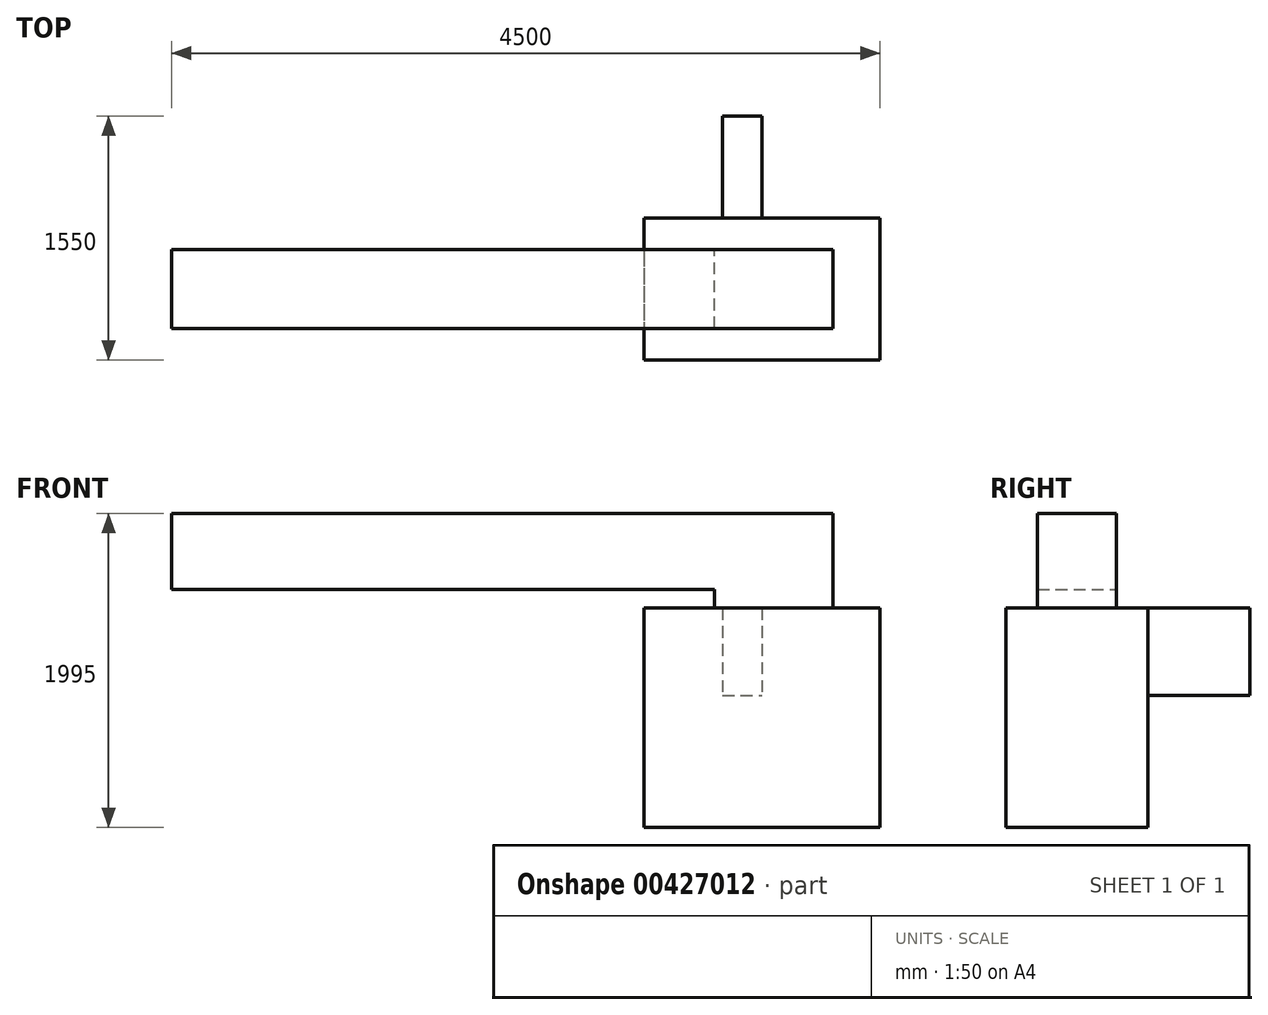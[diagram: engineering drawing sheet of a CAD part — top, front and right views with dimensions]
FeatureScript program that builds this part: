
annotation { "Feature Type Name" : "Feature", "Feature Type Description" : "" }
export const myFeature = defineFeature(function(context is Context, id is Id, definition is map)
    precondition{}
    {
        {
            var Q0;
            Q0=qCreatedBy(makeId("Top.planeOp"),FACE);
            var sketch = newSketch(context, id + "F0", { "sketchPlane" : qUnion([Q0])});
            skLineSegment(sketch, "E0.bottom", {"start": v(-750, 450) * mm, "end": v(750, 450) * mm});
            skLineSegment(sketch, "E0.top", {"start": v(-750, -450) * mm, "end": v(750, -450) * mm});
            skLineSegment(sketch, "E0.left", {"start": v(-750, 450) * mm, "end": v(-750, -450) * mm});
            skLineSegment(sketch, "E0.right", {"start": v(750, 450) * mm, "end": v(750, -450) * mm});
            skSolve(sketch);
        }
        {
            var Q0;
            Q0=makeQuery(id+"F0.imprint","IMPRINT",FACE,{"disambiguationData":[TD([[makeQuery(id+"F0.imprint","IMPRINT",EDGE,{"derivedFrom":sQuery(id+"F0.wireOp",EDGE,"E0.bottom")}),-1.0]])]});
            extrude(context, id + "F1", {"entities" : qUnion([Q0]), "endBound" : BoundingType.SYMMETRIC, "depth" : (840 + 555) * mm});
        }
        {
            var Q0;
            Q0=makeQuery(id+"F1.opExtrude","SWEPT_FACE",FACE,{"disambiguationData":[OSD([sQuery(id+"F0.wireOp",EDGE,"E0.bottom")])]});
            var sketch = newSketch(context, id + "F2", { "sketchPlane" : qUnion([Q0])});
            skLineSegment(sketch, "E1.bottom", {"start": v(250, 697.5) * mm, "end": v(0, 697.5) * mm});
            skLineSegment(sketch, "E1.top", {"start": v(250, 142.5) * mm, "end": v(0, 142.5) * mm});
            skLineSegment(sketch, "E1.left", {"start": v(250, 697.5) * mm, "end": v(250, 142.5) * mm});
            skLineSegment(sketch, "E1.right", {"start": v(0, 697.5) * mm, "end": v(0, 142.5) * mm});
            skSolve(sketch);
        }
        {
            var Q0;
            Q0=makeQuery(id+"F2.imprint","IMPRINT",FACE,{"disambiguationData":[TD([[makeQuery(id+"F2.imprint","IMPRINT",EDGE,{"derivedFrom":sQuery(id+"F2.wireOp",EDGE,"E1.bottom")}),1.0]])]});
            extrude(context, id + "F3", {"entities" : qUnion([Q0]), "depth" : 650 * mm});
        }
        {
            var Q0;
            Q0=makeQuery(id+"F1.opExtrude","CAP_FACE",FACE,{"disambiguationData":[OSD([sQuery(id+"F0.wireOp",EDGE,"E0.bottom"),sQuery(id+"F0.wireOp",EDGE,"E0.top"),sQuery(id+"F0.wireOp",EDGE,"E0.left"),sQuery(id+"F0.wireOp",EDGE,"E0.right")])],"isStart":false});
            var sketch = newSketch(context, id + "F4", { "sketchPlane" : qUnion([Q0])});
            skLineSegment(sketch, "E2.bottom", {"start": v(450, -250) * mm, "end": v(-3750, -250) * mm});
            skLineSegment(sketch, "E2.top", {"start": v(450, 250) * mm, "end": v(-3750, 250) * mm});
            skLineSegment(sketch, "E2.left", {"start": v(450, -250) * mm, "end": v(450, 250) * mm});
            skLineSegment(sketch, "E2.right", {"start": v(-3750, -250) * mm, "end": v(-3750, 250) * mm});
            skSolve(sketch);
        }
        {
            var Q0;
            {var subQ0=sQuery(id+"F4.wireOp",EDGE,"E2.left");Q0=makeQuery(id+"F4.imprint","IMPRINT",FACE,{"disambiguationData":[TD([[makeQuery(id+"F4.imprint","IMPRINT",EDGE,{"derivedFrom":subQ0}),1.0]])]});}
            var Q1;
            {var subQ0=sQuery(id+"F4.wireOp",EDGE,"E2.right");Q1=makeQuery(id+"F4.imprint","IMPRINT",FACE,{"disambiguationData":[TD([[makeQuery(id+"F4.imprint","IMPRINT",EDGE,{"derivedFrom":subQ0}),-1.0]])]});}
            extrude(context, id + "F5", {"entities" : qUnion([Q0, Q1]), "depth" : 600 * mm});
        }
        {
            var Q0;
            Q0=makeQuery(id+"F5.opExtrude","SWEPT_FACE",FACE,{"disambiguationData":[OSD([sQuery(id+"F4.wireOp",EDGE,"E2.top")])]});
            var sketch = newSketch(context, id + "F6", { "sketchPlane" : qUnion([Q0])});
            skLineSegment(sketch, "E3.0.0", {"start": v(-450, 697.5) * mm, "end": v(3750, 697.5) * mm});
            skLineSegment(sketch, "E3.0.1", {"start": v(3750, 697.5) * mm, "end": v(3750, 1297.5) * mm});
            skLineSegment(sketch, "E3.0.2", {"start": v(3750, 1297.5) * mm, "end": v(50, 1297.5) * mm});
            skLineSegment(sketch, "E3.0.3", {"start": v(-450, 797.5) * mm, "end": v(-450, 697.5) * mm});
            skPoint(sketch, "E4.visualSharp", {"position": v(-450, 1297.5) * mm});
            skLineSegment(sketch, "E5", {"start": v(302.9, 697.5) * mm, "end": v(302.9, 815.5) * mm});
            skLineSegment(sketch, "E6", {"start": v(302.9, 815.5) * mm, "end": v(3750, 815.5) * mm});
            skSolve(sketch);
        }
        {
            var Q0;
            {var subQ3=sQuery(id+"F6.wireOp",EDGE,"E5");Q0=makeQuery(id+"F6.imprint","IMPRINT",FACE,{"disambiguationData":[TD([[makeQuery(id+"F6.imprint","IMPRINT",EDGE,{"derivedFrom":subQ3}),-1.0]])]});}
            extrude(context, id + "F7", {"entities" : qUnion([Q0]), "operationType" : NewBodyOperationType.REMOVE, "oppositeDirection" : true, "depth" : 700 * mm});
        }
    });
